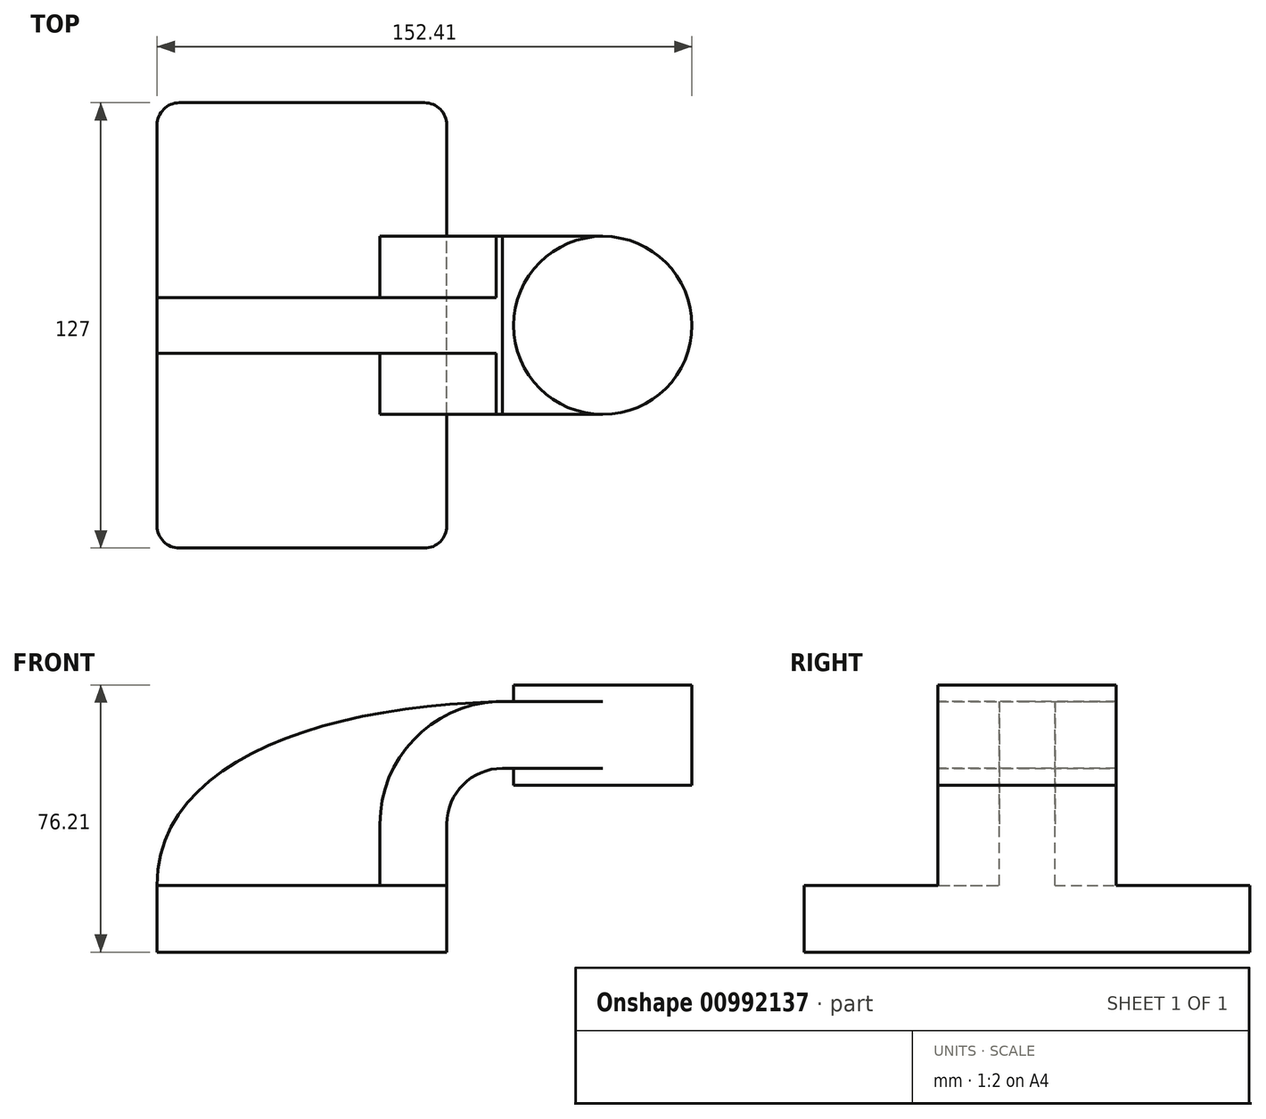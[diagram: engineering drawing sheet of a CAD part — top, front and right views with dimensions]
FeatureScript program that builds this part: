
annotation { "Feature Type Name" : "Feature", "Feature Type Description" : "" }
export const myFeature = defineFeature(function(context is Context, id is Id, definition is map)
    precondition{}
    {
        {
            var Q0;
            Q0=qCreatedBy(makeId("Front.planeOp"),FACE);
            var sketch = newSketch(context, id + "F0", { "sketchPlane" : qUnion([Q0])});
            skLineSegment(sketch, "E0.bottom", {"start": v(-41.28, -9.52) * mm, "end": v(41.28, -9.52) * mm});
            skLineSegment(sketch, "E0.top", {"start": v(-41.28, 9.53) * mm, "end": v(41.28, 9.53) * mm});
            skLineSegment(sketch, "E0.left", {"start": v(-41.28, -9.52) * mm, "end": v(-41.28, 9.53) * mm});
            skLineSegment(sketch, "E0.right", {"start": v(41.28, -9.53) * mm, "end": v(41.28, 9.52) * mm});
            skPoint(sketch, "E0.middle", {"position": v(0, 0) * mm});
            skLineSegment(sketch, "E1.bottom", {"start": v(111.13, 38.1) * mm, "end": v(60.32, 38.1) * mm});
            skLineSegment(sketch, "E1.top", {"start": v(111.13, 66.68) * mm, "end": v(60.32, 66.68) * mm});
            skLineSegment(sketch, "E1.left", {"start": v(111.13, 38.1) * mm, "end": v(111.13, 66.68) * mm});
            skLineSegment(sketch, "E1.right", {"start": v(60.33, 38.1) * mm, "end": v(60.33, 66.68) * mm});
            skPoint(sketch, "E1.middle", {"position": v(85.73, 52.39) * mm});
            skLineSegment(sketch, "E2", {"start": v(41.28, 9.52) * mm, "end": v(41.28, 27) * mm});
            skArc(sketch, "E3", {"start": v(41.28, 27) * mm, "mid": v(45.92, 38.23) * mm, "end": v(57.15, 42.88) * mm});
            skLineSegment(sketch, "E4", {"start": v(57.15, 42.88) * mm, "end": v(75.33, 42.88) * mm});
            skLineSegment(sketch, "E5.0", {"start": v(57.15, 61.93) * mm, "end": v(75.33, 61.93) * mm});
            skArc(sketch, "E5.1", {"start": v(22.23, 27) * mm, "mid": v(32.45, 51.7) * mm, "end": v(57.15, 61.93) * mm});
            skLineSegment(sketch, "E5.2", {"start": v(22.23, 9.52) * mm, "end": v(22.23, 27) * mm});
            skLineSegment(sketch, "E6", {"start": v(85.73, 38.1) * mm, "end": v(85.73, 66.68) * mm});
            skLineSegment(sketch, "E7", {"start": v(75.33, 61.93) * mm, "end": v(85.73, 61.93) * mm});
            skLineSegment(sketch, "E8", {"start": v(75.33, 42.88) * mm, "end": v(85.73, 42.88) * mm});
            skFitSpline(sketch, "E9", {"points": [v(-41.28, 9.53) * mm, v(57.15, 61.93) * mm], "startDerivative": vector(0.31, 106.27) * mm, "endDerivative": vector(155.02, 3.6) * mm});
            skSolve(sketch);
        }
        {
            var Q0;
            Q0=makeQuery(id+"F0.imprint","IMPRINT",FACE,{"disambiguationData":[TD([[makeQuery(id+"F0.imprint","IMPRINT",EDGE,{"derivedFrom":sQuery(id+"F0.wireOp",EDGE,"E0.bottom")}),1.0]])]});
            extrude(context, id + "F1", {"entities" : qUnion([Q0]), "depth" : 127 * mm, "offsetDistance" : 25.4 * mm, "symmetric" : true});
        }
        {
            var Q0;
            {var subQ1=sQuery(id+"F0.wireOp",EDGE,"E2");Q0=makeQuery(id+"F0.imprint","IMPRINT",FACE,{"disambiguationData":[TD([[makeQuery(id+"F0.imprint","IMPRINT",EDGE,{"derivedFrom":subQ1}),1.0]])]});}
            var Q1;
            {var subQ0=sQuery(id+"F0.wireOp",EDGE,"E7");Q1=makeQuery(id+"F0.imprint","IMPRINT",FACE,{"disambiguationData":[TD([[makeQuery(id+"F0.imprint","IMPRINT",EDGE,{"derivedFrom":subQ0}),-1.0]])]});}
            extrude(context, id + "F2", {"entities" : qUnion([Q0, Q1]), "operationType" : NewBodyOperationType.ADD, "depth" : 50.8 * mm, "offsetDistance" : 25.4 * mm, "symmetric" : true});
        }
        {
            var Q0;
            {var subQ3=sQuery(id+"F0.wireOp",EDGE,"E5.2");Q0=makeQuery(id+"F0.imprint","IMPRINT",FACE,{"disambiguationData":[TD([[makeQuery(id+"F0.imprint","IMPRINT",EDGE,{"derivedFrom":subQ3}),1.0]])]});}
            extrude(context, id + "F3", {"entities" : qUnion([Q0]), "operationType" : NewBodyOperationType.ADD, "depth" : 15.88 * mm, "offsetDistance" : 25.4 * mm, "symmetric" : true});
        }
        {
            var Q0;
            {var subQ0=sQuery(id+"F0.wireOp",EDGE,"E1.left");Q0=makeQuery(id+"F0.imprint","IMPRINT",FACE,{"disambiguationData":[TD([[makeQuery(id+"F0.imprint","IMPRINT",EDGE,{"derivedFrom":subQ0}),1.0]])]});}
            var Q1;
            Q1=sQuery(id+"F0.wireOp",EDGE,"E6");
            revolve(context, id + "F4", {"operationType" : NewBodyOperationType.ADD, "surfaceOperationType" : NewSurfaceOperationType.NEW, "entities" : qUnion([Q0]), "axis" : qUnion([Q1]), "revolveType" : RevolveType.FULL});
        }
        {
            var Q0;
            Q0=makeQuery(id+"F1.opExtrude","CAP_EDGE",EDGE,{"disambiguationData":[OSD([sQuery(id+"F0.wireOp",EDGE,"E0.right")])],"isStart":false});
            var Q1;
            Q1=makeQuery(id+"F1.opExtrude","CAP_EDGE",EDGE,{"disambiguationData":[OSD([sQuery(id+"F0.wireOp",EDGE,"E0.left")])],"isStart":false});
            var Q2;
            Q2=makeQuery(id+"F1.opExtrude","CAP_EDGE",EDGE,{"disambiguationData":[OSD([sQuery(id+"F0.wireOp",EDGE,"E0.right")])],"isStart":true});
            var Q3;
            Q3=makeQuery(id+"F1.opExtrude","CAP_EDGE",EDGE,{"disambiguationData":[OSD([sQuery(id+"F0.wireOp",EDGE,"E0.left")])],"isStart":true});
            fillet(context, id + "F5", {"entities" : qUnion([Q0, Q1, Q2, Q3]), "radius" : 6.35 * mm, "tangentPropagation" : true, "allowEdgeOverflow" : false});
        }
    });
